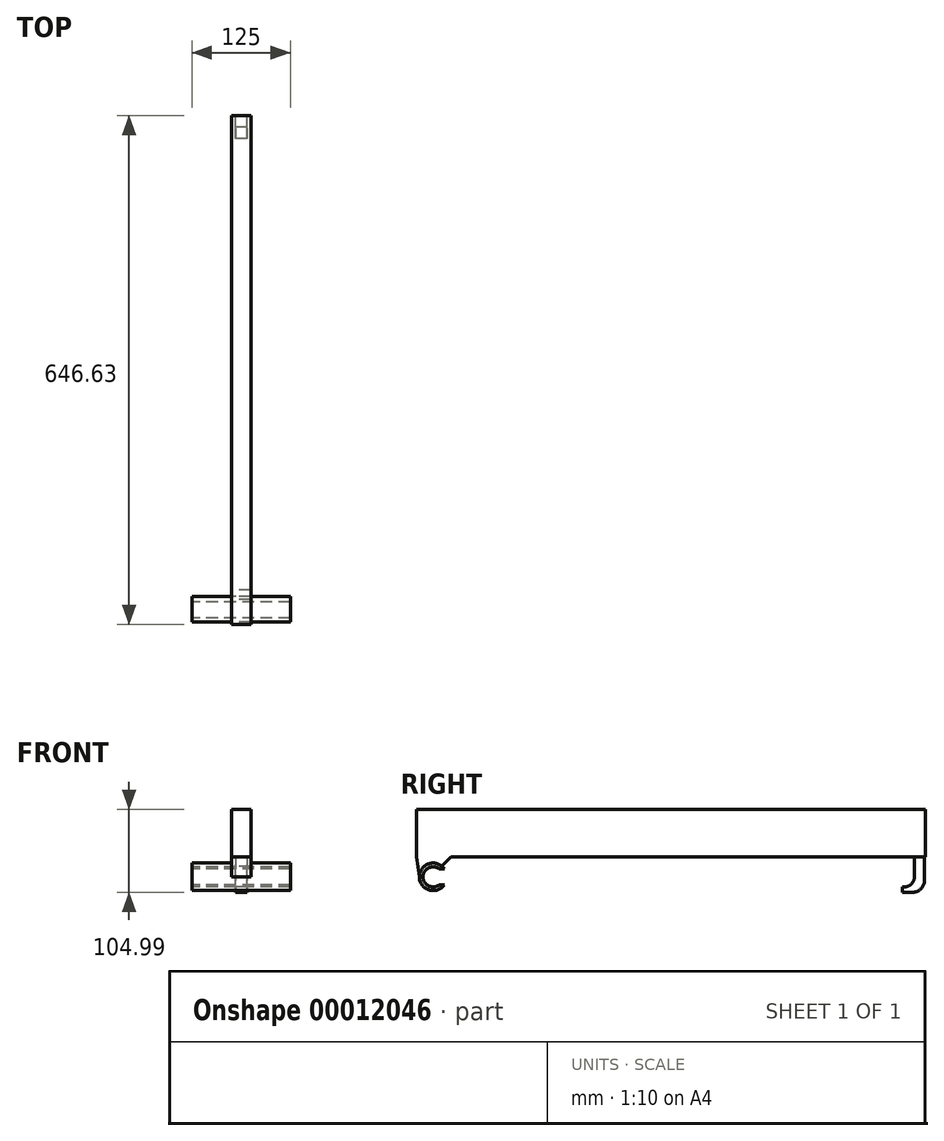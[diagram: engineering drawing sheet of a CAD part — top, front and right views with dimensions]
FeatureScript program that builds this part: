
annotation { "Feature Type Name" : "Feature", "Feature Type Description" : "" }
export const myFeature = defineFeature(function(context is Context, id is Id, definition is map)
    precondition{}
    {
        {
            var Q0;
            Q0=qCreatedBy(makeId("Right.planeOp"),FACE);
            var sketch = newSketch(context, id + "F0", { "sketchPlane" : qUnion([Q0])});
            skArc(sketch, "E0", {"start": v(7.83, 10) * mm, "mid": v(-12.7, 0) * mm, "end": v(7.83, -10) * mm});
            skArc(sketch, "E1", {"start": v(14.36, 10) * mm, "mid": v(-17.5, 0) * mm, "end": v(14.36, -10) * mm});
            skLineSegment(sketch, "E2.0", {"start": v(7.83, -10) * mm, "end": v(14.36, -10) * mm});
            skLineSegment(sketch, "E3.0", {"start": v(7.83, 10) * mm, "end": v(14.36, 10) * mm});
            skSolve(sketch);
        }
        {
            var Q0;
            Q0=makeQuery(id+"F0.imprint","IMPRINT",FACE,{"disambiguationData":[TD([[makeQuery(id+"F0.imprint","IMPRINT",EDGE,{"derivedFrom":sQuery(id+"F0.wireOp",EDGE,"E0")}),-1.0]])]});
            extrude(context, id + "F1", {"entities" : qUnion([Q0]), "depth" : 125 * mm, "symmetric" : true});
        }
        {
            var Q0;
            Q0=qCreatedBy(makeId("Right.planeOp"),FACE);
            var sketch = newSketch(context, id + "F2", { "sketchPlane" : qUnion([Q0])});
            skLineSegment(sketch, "E4.bottom", {"start": v(22.79, 25.4) * mm, "end": v(625.47, 25.4) * mm});
            skLineSegment(sketch, "E4.top", {"start": v(-21.16, 85.4) * mm, "end": v(625.47, 85.4) * mm});
            skLineSegment(sketch, "E4.left", {"start": v(-21.16, 25.4) * mm, "end": v(-21.16, 85.4) * mm});
            skLineSegment(sketch, "E4.right", {"start": v(625.47, 25.4) * mm, "end": v(625.47, 85.4) * mm});
            skCircle(sketch, "E5", {"center": v(598.8, 0) * mm, "radius": 12.7 * mm, "construction": true});
            skPoint(sketch, "E6.orphan", {"position": v(611.5, 0) * mm});
            skLineSegment(sketch, "E7", {"start": v(-21.16, 25.4) * mm, "end": v(-17.5, 0) * mm});
            skLineSegment(sketch, "E8", {"start": v(11.03, 13.58) * mm, "end": v(22.79, 25.4) * mm});
            skArc(sketch, "E9", {"start": v(11.03, 13.58) * mm, "mid": v(-7.52, 15.8) * mm, "end": v(-17.5, 0) * mm});
            skPoint(sketch, "E10.orphan", {"position": v(-17.5, 0) * mm});
            skSolve(sketch);
        }
        {
            var Q0;
            Q0 = qSketchRegion(id + "F2", true);
            extrude(context, id + "F3", {"entities" : qUnion([Q0]), "operationType" : NewBodyOperationType.ADD, "depth" : 25 * mm, "symmetric" : true});
        }
        {
            var Q0;
            Q0=qCreatedBy(makeId("Right.planeOp"),FACE);
            var sketch = newSketch(context, id + "F4", { "sketchPlane" : qUnion([Q0])});
            skArc(sketch, "E11", {"start": v(596.4, -12.47) * mm, "mid": v(606.9, -9.79) * mm, "end": v(611.5, 0) * mm});
            skLineSegment(sketch, "E12", {"start": v(624.22, 26.26) * mm, "end": v(624.22, -4.6) * mm});
            skLineSegment(sketch, "E13", {"start": v(609.22, -19.6) * mm, "end": v(596.4, -19.6) * mm});
            skLineSegment(sketch, "E14", {"start": v(611.5, 0) * mm, "end": v(611.5, 26.26) * mm});
            skPoint(sketch, "E15.visualSharp", {"position": v(624.22, -19.6) * mm});
            skArc(sketch, "E15.filletArc", {"start": v(609.22, -19.6) * mm, "mid": v(619.83, -15.2) * mm, "end": v(624.22, -4.6) * mm});
            skLineSegment(sketch, "E16", {"start": v(611.5, 26.26) * mm, "end": v(624.22, 26.26) * mm});
            skPoint(sketch, "E17.orphan", {"position": v(611.5, 52.51) * mm});
            skLineSegment(sketch, "E18", {"start": v(596.4, -12.47) * mm, "end": v(596.4, -19.6) * mm});
            skSolve(sketch);
        }
        {
            var Q0;
            Q0 = qSketchRegion(id + "F4", true);
            extrude(context, id + "F5", {"entities" : qUnion([Q0]), "operationType" : NewBodyOperationType.ADD, "depth" : 15 * mm, "symmetric" : true});
        }
    });
